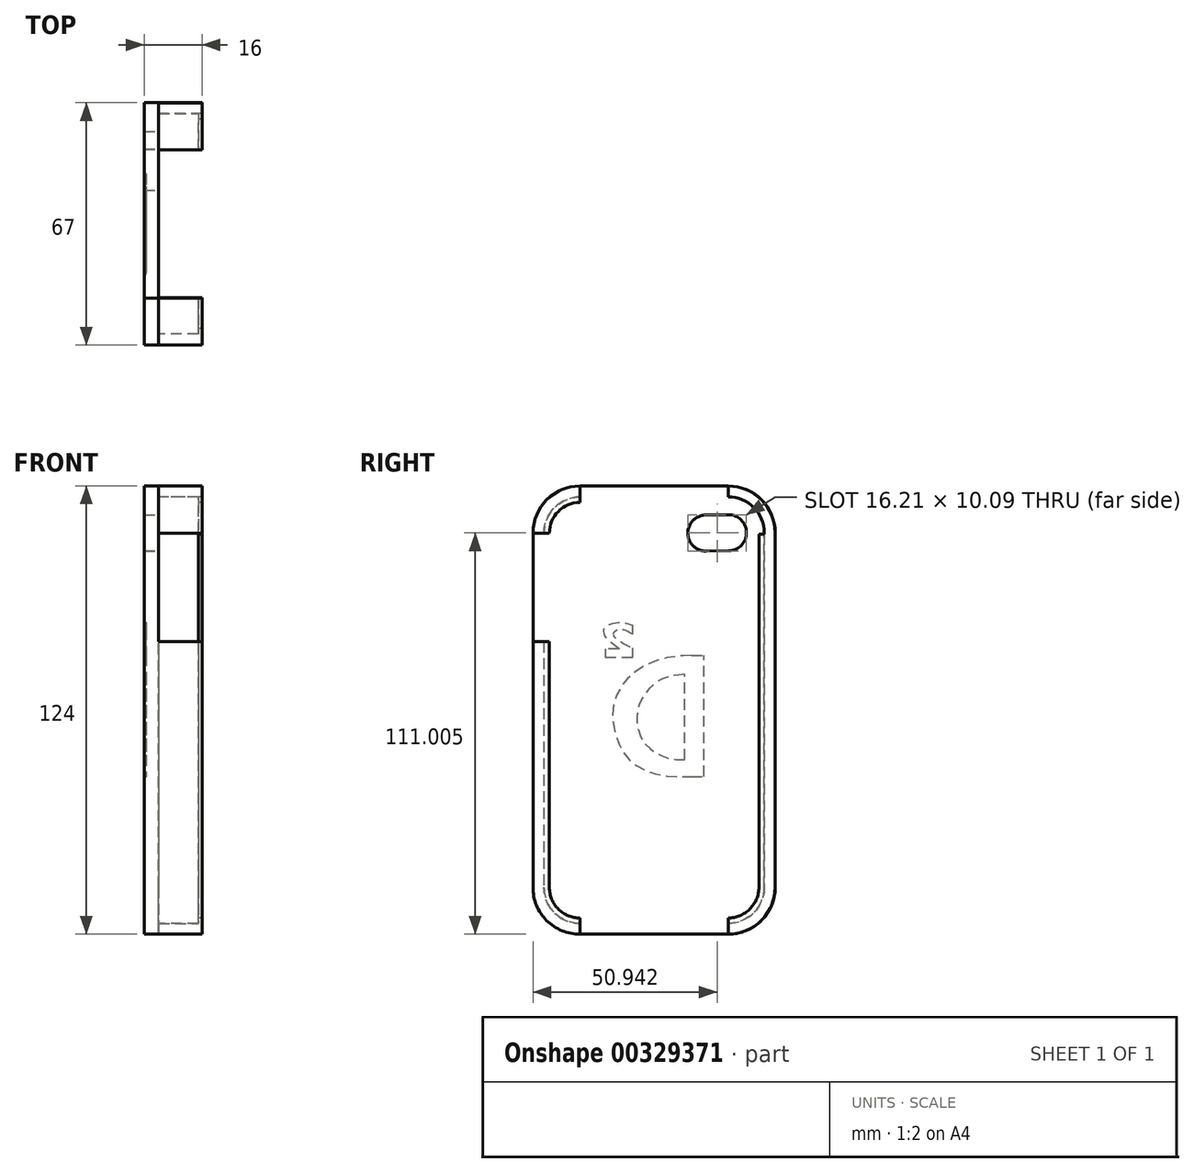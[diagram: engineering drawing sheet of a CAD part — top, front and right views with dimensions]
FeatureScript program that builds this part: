
annotation { "Feature Type Name" : "Feature", "Feature Type Description" : "" }
export const myFeature = defineFeature(function(context is Context, id is Id, definition is map)
    precondition{}
    {
        {
            var Q0;
            Q0=qCreatedBy(makeId("Right.planeOp"),FACE);
            var sketch = newSketch(context, id + "F0", { "sketchPlane" : qUnion([Q0])});
            skLineSegment(sketch, "E0.rect.bottom", {"start": v(20.5, 62) * mm, "end": v(-20.5, 62) * mm});
            skLineSegment(sketch, "E0.rect.top", {"start": v(20.5, -62) * mm, "end": v(-20.5, -62) * mm});
            skLineSegment(sketch, "E0.rect.left", {"start": v(33.5, 49) * mm, "end": v(33.5, -49) * mm});
            skLineSegment(sketch, "E0.rect.right", {"start": v(-33.5, 49) * mm, "end": v(-33.5, -49) * mm});
            skPoint(sketch, "E0.rect.middle", {"position": v(0, 0) * mm});
            skPoint(sketch, "E1.visualSharp", {"position": v(-33.5, 62) * mm});
            skArc(sketch, "E1.filletArc", {"start": v(-20.5, 62) * mm, "mid": v(-29.7, 58.2) * mm, "end": v(-33.5, 49) * mm});
            skPoint(sketch, "E2.visualSharp", {"position": v(-33.5, -62) * mm});
            skArc(sketch, "E2.filletArc", {"start": v(-33.5, -49) * mm, "mid": v(-29.7, -58.2) * mm, "end": v(-20.5, -62) * mm});
            skPoint(sketch, "E3.visualSharp", {"position": v(33.5, 62) * mm});
            skArc(sketch, "E3.filletArc", {"start": v(33.5, 49) * mm, "mid": v(29.7, 58.2) * mm, "end": v(20.5, 62) * mm});
            skPoint(sketch, "E4.visualSharp", {"position": v(33.5, -62) * mm});
            skArc(sketch, "E4.filletArc", {"start": v(20.5, -62) * mm, "mid": v(29.7, -58.2) * mm, "end": v(33.5, -49) * mm});
            skSolve(sketch);
        }
        {
            var Q0;
            Q0=qSketchRegion(id+"F0",true);
            extrude(context, id + "F1", {"entities" : qUnion([Q0]), "depth" : 4 * mm});
        }
        {
            var Q0;
            Q0=qCreatedBy(makeId("Right.planeOp"),FACE);
            var sketch = newSketch(context, id + "F2", { "sketchPlane" : qUnion([Q0])});
            skArc(sketch, "E5", {"start": v(20.7, 44.05) * mm, "mid": v(25.55, 49.12) * mm, "end": v(20.55, 54.05) * mm});
            skLineSegment(sketch, "E6", {"start": v(20.55, 54.05) * mm, "end": v(14.26, 53.96) * mm});
            skLineSegment(sketch, "E7", {"start": v(20.7, 44.05) * mm, "end": v(14.4, 43.96) * mm});
            skArc(sketch, "E8", {"start": v(14.26, 53.96) * mm, "mid": v(9.34, 48.89) * mm, "end": v(14.4, 43.96) * mm});
            skLineSegment(sketch, "E9", {"start": v(14.26, 53.96) * mm, "end": v(14.4, 43.96) * mm, "construction": true});
            skLineSegment(sketch, "E10", {"start": v(20.55, 54.05) * mm, "end": v(20.7, 44.05) * mm, "construction": true});
            skSolve(sketch);
        }
        {
            var Q0;
            Q0=makeQuery(id+"F2.imprint","IMPRINT",FACE,{"disambiguationData":[TD([[makeQuery(id+"F2.imprint","IMPRINT",EDGE,{"derivedFrom":sQuery(id+"F2.wireOp",EDGE,"E5")}),1.0]])]});
            extrude(context, id + "F3", {"entities" : qUnion([Q0]), "operationType" : NewBodyOperationType.REMOVE, "oppositeDirection" : true, "depth" : 25.4 * mm, "hasSecondDirection" : true, "secondDirectionOppositeDirection" : false, "secondDirectionDepth" : 33.72 * mm});
        }
        {
            var Q0;
            Q0=qCreatedBy(makeId("Right.planeOp"),FACE);
            var sketch = newSketch(context, id + "F4", { "sketchPlane" : qUnion([Q0])});
            skLineSegment(sketch, "E11.bottom", {"start": v(13.8, 15.16) * mm, "end": v(10.36, 15.16) * mm});
            skLineSegment(sketch, "E11.top", {"start": v(13.8, -18.37) * mm, "end": v(10.36, -18.37) * mm});
            skLineSegment(sketch, "E11.left", {"start": v(13.8, 15.16) * mm, "end": v(13.8, -18.37) * mm});
            skFitSpline(sketch, "E12", {"points": [v(10.36, 15.16) * mm, v(2.8, 14.3) * mm, v(-5.23, 10.55) * mm, v(-10.98, 2.35) * mm, v(-10.02, -8.63) * mm, v(-3.92, -15.96) * mm, v(10.36, -18.37) * mm], "startDerivative": vector(-52.68, -2.78) * mm, "endDerivative": vector(80, 5.61) * mm});
            skLineSegment(sketch, "E13", {"start": v(8.44, 9.88) * mm, "end": v(8.44, -13.75) * mm});
            skFitSpline(sketch, "E14", {"points": [v(8.44, 9.88) * mm, v(3.13, 8.92) * mm, v(-1.4, 5.87) * mm, v(-4.55, 0) * mm, v(-4.02, -6.6) * mm, v(-0.62, -11.04) * mm, v(8.44, -13.75) * mm], "startDerivative": vector(-36.15, -4.17) * mm, "endDerivative": vector(56.67, 3.08) * mm});
            skLineSegment(sketch, "E15", {"start": v(-5.94, 23.49) * mm, "end": v(-5.94, 20.96) * mm});
            skFitSpline(sketch, "E16", {"points": [v(-5.94, 20.96) * mm, v(-9.35, 22.28) * mm, v(-11.32, 20.96) * mm, v(-5.94, 17.12) * mm], "startDerivative": vector(-10.5, 6.63) * mm, "endDerivative": vector(19.02, -9.58) * mm});
            skLineSegment(sketch, "E17", {"start": v(-5.94, 17.12) * mm, "end": v(-5.94, 14.6) * mm});
            skLineSegment(sketch, "E18", {"start": v(-5.94, 14.6) * mm, "end": v(-13.52, 14.6) * mm});
            skLineSegment(sketch, "E19", {"start": v(-13.52, 14.6) * mm, "end": v(-13.52, 16.9) * mm});
            skLineSegment(sketch, "E20", {"start": v(-13.52, 16.9) * mm, "end": v(-9.57, 16.9) * mm});
            skFitSpline(sketch, "E21", {"points": [v(-9.57, 16.9) * mm, v(-13.52, 20.52) * mm, v(-13.52, 22.94) * mm, v(-9.57, 24.26) * mm, v(-5.94, 23.49) * mm], "startDerivative": vector(-16.46, 11.92) * mm, "endDerivative": vector(13.67, -4.73) * mm});
            skSolve(sketch);
        }
        {
            var Q0;
            Q0=qSketchRegion(id+"F4",true);
            extrude(context, id + "F5", {"entities" : qUnion([Q0]), "operationType" : NewBodyOperationType.REMOVE, "depth" : 0.5 * mm, "hasSecondDirection" : true, "secondDirectionOppositeDirection" : true, "secondDirectionDepth" : 10 * mm});
        }
        {
            var Q0;
            Q0=qCreatedBy(makeId("Right.planeOp"),FACE);
            var sketch = newSketch(context, id + "F6", { "sketchPlane" : qUnion([Q0])});
            skLineSegment(sketch, "E22", {"start": v(-30.46, 18.92) * mm, "end": v(-33.5, 18.92) * mm});
            skLineSegment(sketch, "E23", {"start": v(-33.5, 18.92) * mm, "end": v(-33.5, -49) * mm});
            skLineSegment(sketch, "E24", {"start": v(-33.5, -49) * mm, "end": v(-30.46, -49) * mm});
            skLineSegment(sketch, "E25", {"start": v(-30.46, -49) * mm, "end": v(-30.46, 18.92) * mm});
            skSolve(sketch);
        }
        {
            var Q0;
            Q0=qSketchRegion(id+"F6",true);
            extrude(context, id + "F7", {"entities" : qUnion([Q0]), "operationType" : NewBodyOperationType.ADD, "depth" : 16 * mm});
        }
        {
            var Q0;
            Q0=qCreatedBy(makeId("Right.planeOp"),FACE);
            var sketch = newSketch(context, id + "F8", { "sketchPlane" : qUnion([Q0])});
            skLineSegment(sketch, "E26", {"start": v(-33.5, -49) * mm, "end": v(-30.46, -49) * mm});
            skLineSegment(sketch, "E27", {"start": v(-20.5, -59) * mm, "end": v(-20.5, -62) * mm});
            skArc(sketch, "E28", {"start": v(-30.46, -49) * mm, "mid": v(-27.56, -56.07) * mm, "end": v(-20.5, -59) * mm});
            skArc(sketch, "E29", {"start": v(-33.5, -49) * mm, "mid": v(-29.7, -58.2) * mm, "end": v(-20.5, -62) * mm});
            skSolve(sketch);
        }
        {
            var Q0;
            Q0=qSketchRegion(id+"F8",true);
            extrude(context, id + "F9", {"entities" : qUnion([Q0]), "operationType" : NewBodyOperationType.ADD, "depth" : 16 * mm});
        }
        {
            var Q0;
            Q0=qCreatedBy(makeId("Right.planeOp"),FACE);
            var sketch = newSketch(context, id + "F10", { "sketchPlane" : qUnion([Q0])});
            skLineSegment(sketch, "E30", {"start": v(-30.47, 48.93) * mm, "end": v(-33.5, 48.93) * mm});
            skLineSegment(sketch, "E31", {"start": v(-20.5, 62) * mm, "end": v(-20.5, 58.97) * mm});
            skArc(sketch, "E32", {"start": v(-20.5, 58.97) * mm, "mid": v(-27.55, 56) * mm, "end": v(-30.47, 48.93) * mm});
            skArc(sketch, "E33", {"start": v(-20.5, 62) * mm, "mid": v(-29.7, 58.15) * mm, "end": v(-33.5, 48.93) * mm});
            skSolve(sketch);
        }
        {
            var Q0;
            Q0=qSketchRegion(id+"F10",true);
            extrude(context, id + "F11", {"entities" : qUnion([Q0]), "operationType" : NewBodyOperationType.ADD, "depth" : 16 * mm});
        }
        {
            var Q0;
            Q0=qCreatedBy(makeId("Right.planeOp"),FACE);
            var sketch = newSketch(context, id + "F12", { "sketchPlane" : qUnion([Q0])});
            skLineSegment(sketch, "E34", {"start": v(20.49, -62) * mm, "end": v(20.49, -59) * mm});
            skLineSegment(sketch, "E35", {"start": v(33.5, -49) * mm, "end": v(30.5, -49) * mm});
            skArc(sketch, "E36", {"start": v(20.49, -59) * mm, "mid": v(27.55, -56.06) * mm, "end": v(30.5, -49) * mm});
            skArc(sketch, "E37", {"start": v(20.49, -62) * mm, "mid": v(29.67, -58.19) * mm, "end": v(33.5, -49) * mm});
            skSolve(sketch);
        }
        {
            var Q0;
            Q0=qSketchRegion(id+"F12",true);
            extrude(context, id + "F13", {"entities" : qUnion([Q0]), "operationType" : NewBodyOperationType.ADD, "depth" : 16 * mm});
        }
        {
            var Q0;
            Q0=qCreatedBy(makeId("Right.planeOp"),FACE);
            var sketch = newSketch(context, id + "F14", { "sketchPlane" : qUnion([Q0])});
            skLineSegment(sketch, "E38", {"start": v(33.46, 49) * mm, "end": v(30.5, 49) * mm});
            skLineSegment(sketch, "E39", {"start": v(20.5, 62) * mm, "end": v(20.5, 58.99) * mm});
            skArc(sketch, "E40", {"start": v(33.46, 49) * mm, "mid": v(29.66, 58.17) * mm, "end": v(20.5, 62) * mm});
            skArc(sketch, "E41", {"start": v(30.5, 49) * mm, "mid": v(27.55, 56.05) * mm, "end": v(20.5, 58.99) * mm});
            skSolve(sketch);
        }
        {
            var Q0;
            Q0=qSketchRegion(id+"F14",true);
            extrude(context, id + "F15", {"entities" : qUnion([Q0]), "operationType" : NewBodyOperationType.ADD, "depth" : 16 * mm});
        }
        {
            var Q0;
            Q0=qCreatedBy(makeId("Right.planeOp"),FACE);
            var sketch = newSketch(context, id + "F16", { "sketchPlane" : qUnion([Q0])});
            skLineSegment(sketch, "E42", {"start": v(30.5, -49) * mm, "end": v(33.49, -49) * mm});
            skLineSegment(sketch, "E43", {"start": v(33.49, -49) * mm, "end": v(33.49, 49) * mm});
            skLineSegment(sketch, "E44", {"start": v(33.49, 49) * mm, "end": v(30.5, 49) * mm});
            skLineSegment(sketch, "E45", {"start": v(30.5, 49) * mm, "end": v(30.5, -49) * mm});
            skSolve(sketch);
        }
        {
            var Q0;
            Q0=qSketchRegion(id+"F16",true);
            extrude(context, id + "F17", {"entities" : qUnion([Q0]), "operationType" : NewBodyOperationType.ADD, "depth" : 16 * mm});
        }
        {
            var Q0;
            Q0=qCreatedBy(makeId("Right.planeOp"),FACE);
            var sketch = newSketch(context, id + "F18", { "sketchPlane" : qUnion([Q0])});
            skLineSegment(sketch, "E46", {"start": v(-30.46, 18.92) * mm, "end": v(-30.46, -49.07) * mm});
            skLineSegment(sketch, "E47", {"start": v(-30.46, -49.07) * mm, "end": v(-28.96, -49.07) * mm});
            skLineSegment(sketch, "E48", {"start": v(-28.96, -49.07) * mm, "end": v(-28.96, 18.92) * mm});
            skLineSegment(sketch, "E49", {"start": v(-28.96, 18.92) * mm, "end": v(-30.46, 18.92) * mm});
            skLineSegment(sketch, "E50", {"start": v(-20.5, -59) * mm, "end": v(-20.5, -57.5) * mm});
            skArc(sketch, "E51", {"start": v(-30.46, -49.07) * mm, "mid": v(-27.53, -56.1) * mm, "end": v(-20.5, -59) * mm});
            skArc(sketch, "E52", {"start": v(-28.96, -49.07) * mm, "mid": v(-26.47, -55.04) * mm, "end": v(-20.5, -57.5) * mm});
            skLineSegment(sketch, "E53", {"start": v(-30.47, 48.93) * mm, "end": v(-28.97, 48.93) * mm});
            skLineSegment(sketch, "E54", {"start": v(-20.5, 58.97) * mm, "end": v(-20.5, 57.47) * mm});
            skArc(sketch, "E55", {"start": v(-20.5, 58.97) * mm, "mid": v(-27.55, 56) * mm, "end": v(-30.47, 48.93) * mm});
            skArc(sketch, "E56", {"start": v(-20.5, 57.47) * mm, "mid": v(-26.5, 54.95) * mm, "end": v(-28.97, 48.93) * mm});
            skLineSegment(sketch, "E57", {"start": v(30.5, 48.62) * mm, "end": v(29, 48.62) * mm});
            skLineSegment(sketch, "E58", {"start": v(30.5, -49) * mm, "end": v(29, -49) * mm});
            skLineSegment(sketch, "E59", {"start": v(29, -49) * mm, "end": v(29, 48.62) * mm});
            skLineSegment(sketch, "E60", {"start": v(30.5, 48.62) * mm, "end": v(30.5, -49) * mm});
            skLineSegment(sketch, "E61", {"start": v(20.49, -59) * mm, "end": v(20.49, -57.5) * mm});
            skArc(sketch, "E62", {"start": v(20.49, -59) * mm, "mid": v(27.54, -56.06) * mm, "end": v(30.5, -49) * mm});
            skArc(sketch, "E63", {"start": v(20.49, -57.5) * mm, "mid": v(26.5, -55.02) * mm, "end": v(29, -49) * mm});
            skSolve(sketch);
        }
        {
            var Q0;
            Q0=qSketchRegion(id+"F18",true);
            extrude(context, id + "F19", {"entities" : qUnion([Q0]), "operationType" : NewBodyOperationType.ADD, "depth" : 16 * mm, "hasSecondDirection" : true, "secondDirectionOppositeDirection" : false, "secondDirectionDepth" : 15 * mm});
        }
    });
